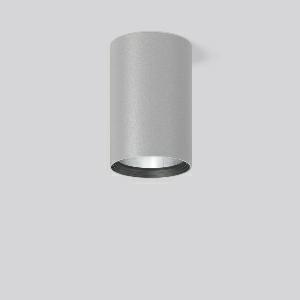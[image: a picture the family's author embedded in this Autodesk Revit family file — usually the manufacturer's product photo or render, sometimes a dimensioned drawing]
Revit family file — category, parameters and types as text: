
# Revit family: heledon_maxi_a_931218_004_76_66a5
name_source: partatom
category: Lighting Fixtures
units: mm (PartAtom-declared; Revit-internal decimal feet)

## family parameters
Cut with Voids When Loaded = No
Host = Face
Light Source = No
Part Type = Normal
Room Calculation Point = No
Round Connector Dimension = Use Diameter
Shared = No

## types (1)
- HELEDON maxi A (1 x LED Modul 930, 3350 lm, 3000)
    Apparent Load = 25 VA
    Approval mark = CE
    CIE Flux Codes = 100 100 100 100 100
    Color Rendering = 90
    Color Temperature = 3000
    Default Elevation = 1800 mm
    Description = Series: HELEDON maxi
Cylindrical surface-mounted downlight. Housing: die-cast aluminium, powder-coated. Internal ceiling frame polycarbonate with bayonet mounting. Black plastic ring and recessed LED to prevent glare from the side. Optical assembly with reflector made of MIRO-Silver with 98% total light reflection for outstanding efficiency - can be changed without tools. Best colour rendering index Ra>90. Suitable for Ceiling mounting. Easy installation with a separate ceiling frame with bayonet mounting and plug connection. Driver integrated. Connected via plug-in connector. High quality converter without flickering and stroboscopic effect. The following accessories can be mounted without use of tools: interchangeable lenses, decorative glasses, honeycomb louvre, clear and frosted diffusers, white interchangeable plastic ring. 
Colour: silver
Diameter: 123 mm
Height: 183 mm
Lamp: LED
Socket: without socket
Colour temperature: 3000K
Colour rendering index (CRI): 92
System power: 25 W
Rated luminous flux: 3350 lm
Luminous efficiency: 134 lm/W
Control gear: Converter, dimmable, DALI
Protection class: I
Type of protection: IP 20
    Height = 183 mm
    Lamp = 1 x LED Modul 930
    Lamp Light Flux = 3350 lm
    Lamp count = 1
    Length = 123 mm
    Lifetime = 50000 h
    Luminous efficacy = 134 lm/W
    Manufacturer = RZB
    ModVariant = No
    Model = 931218.004.76
    Mounting Place = Ceiling
    Mounting Type = Surface mounted
    Number of Poles = 1
    OnlyDefault = Yes
    Power Factor = 1
    Product Name = HELEDON maxi A
    Product group = Surface mounted downlights
    ProductGroupID = 302
    Protection Class = Protection class I
    Protection Degree = IP 20
    RLX_Detail_Level = 1
    RLX_Emergency_Light_Flux = 0 lm
    RLX_Emergency_Type = 0
    RLX_Emergency_Type_DB = No
    RlxData = <blob elided: 100685 chars, md5=64442dc6>
    Socket = socket
    Standby Power = 0 W
    System Light Flux = 3350 lm
    System Power = 25 W
    Type Comments = Product without accessories
    Type Image = 931192.004.jpg
    URL = http://relux.com
    VarID = ---
    Voltage = 230 V
    Voltage Range = 220-240 V
    Weight = 0.00 kg
    Width = 0 mm  [stored 0 ft]

note: [stored X ft] marks values corroborated as IEEE doubles in the binary element streams (Revit-internal decimal feet)

## geometry (parser evidence)
native form markers: Blend x4, Sweep x10
no freeform markers — native parametric forms only
